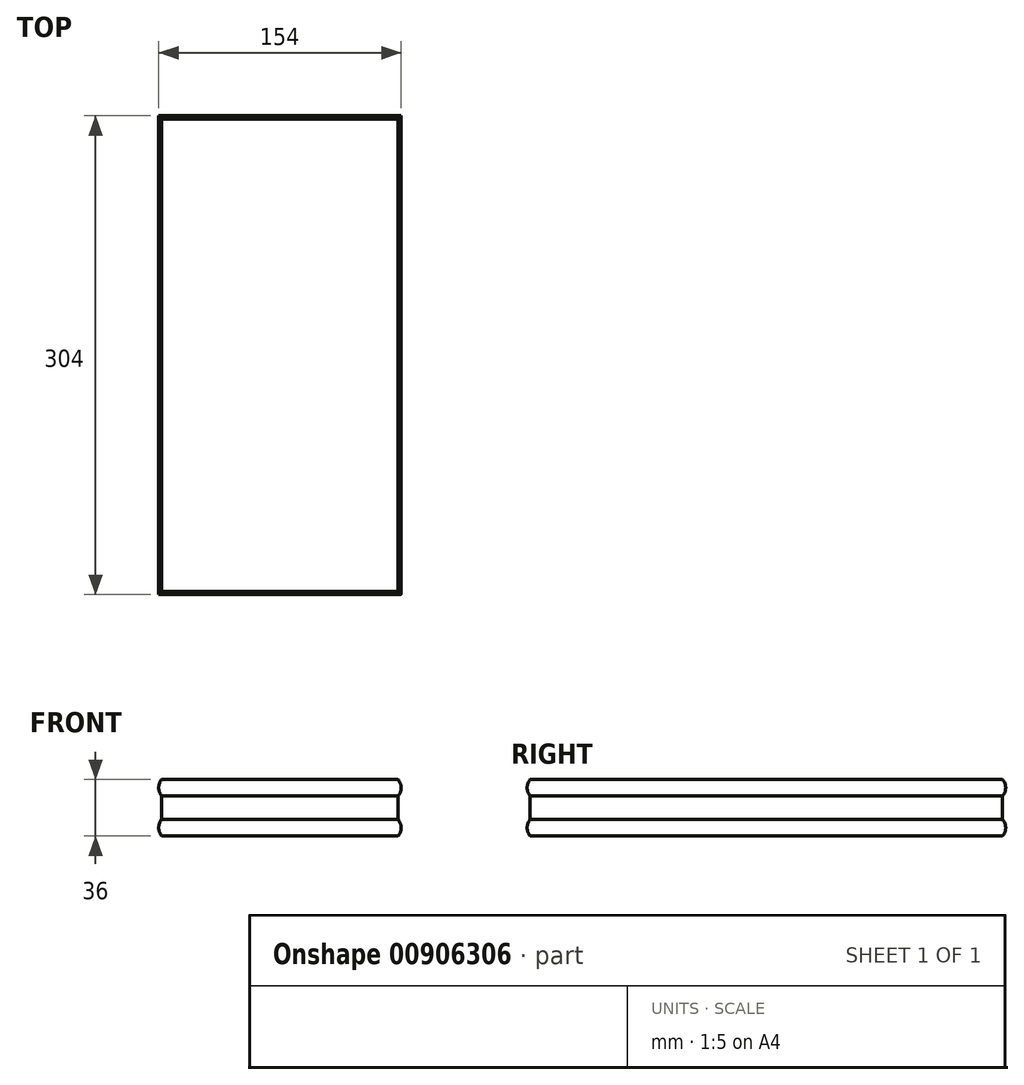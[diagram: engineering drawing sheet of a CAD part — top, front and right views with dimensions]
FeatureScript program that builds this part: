
annotation { "Feature Type Name" : "Feature", "Feature Type Description" : "" }
export const myFeature = defineFeature(function(context is Context, id is Id, definition is map)
    precondition{}
    {
        {
            var Q0;
            Q0=qCreatedBy(makeId("Top.planeOp"),FACE);
            var sketch = newSketch(context, id + "F0", { "sketchPlane" : qUnion([Q0])});
            skLineSegment(sketch, "E0.bottom", {"start": v(-75, -50) * mm, "end": v(75, -50) * mm});
            skLineSegment(sketch, "E0.top", {"start": v(-75, 250) * mm, "end": v(75, 250) * mm});
            skLineSegment(sketch, "E0.left", {"start": v(-75, -50) * mm, "end": v(-75, 250) * mm});
            skLineSegment(sketch, "E0.right", {"start": v(75, -50) * mm, "end": v(75, 250) * mm});
            skSolve(sketch);
        }
        {
            var Q0;
            Q0=qCreatedBy(makeId("Front.planeOp"),FACE);
            var sketch = newSketch(context, id + "F1", { "sketchPlane" : qUnion([Q0])});
            skLineSegment(sketch, "E1", {"start": v(-75, 0) * mm, "end": v(-75, 36) * mm});
            skLineSegment(sketch, "E2", {"start": v(-75, 0) * mm, "end": v(0, 0) * mm});
            skLineSegment(sketch, "E3", {"start": v(0, 0) * mm, "end": v(0, 36) * mm});
            skLineSegment(sketch, "E4", {"start": v(0, 36) * mm, "end": v(-75, 36) * mm});
            skArc(sketch, "E5", {"start": v(-75, 10.58) * mm, "mid": v(-77, 5.3) * mm, "end": v(-75, 0) * mm});
            skArc(sketch, "E6", {"start": v(-75, 36) * mm, "mid": v(-77, 30.7) * mm, "end": v(-75, 25.42) * mm});
            skSolve(sketch);
        }
        {
            var Q0;
            {var subQ0=sQuery(id+"F1.wireOp",EDGE,"E2");Q0=makeQuery(id+"F1.imprint","IMPRINT",FACE,{"disambiguationData":[TD([[makeQuery(id+"F1.imprint","IMPRINT",EDGE,{"derivedFrom":subQ0}),1.0]])]});}
            var Q1;
            {var subQ0=sQuery(id+"F1.wireOp",EDGE,"E6");Q1=makeQuery(id+"F1.imprint","IMPRINT",FACE,{"disambiguationData":[TD([[makeQuery(id+"F1.imprint","IMPRINT",EDGE,{"derivedFrom":subQ0}),1.0]])]});}
            var Q2;
            {var subQ0=sQuery(id+"F1.wireOp",EDGE,"E5");Q2=makeQuery(id+"F1.imprint","IMPRINT",FACE,{"disambiguationData":[TD([[makeQuery(id+"F1.imprint","IMPRINT",EDGE,{"derivedFrom":subQ0}),1.0]])]});}
            var Q3;
            Q3=sQuery(id+"F0.wireOp",EDGE,"E0.left");
            var Q4;
            Q4=sQuery(id+"F0.wireOp",EDGE,"E0.bottom");
            var Q5;
            Q5=sQuery(id+"F0.wireOp",EDGE,"E0.right");
            var Q6;
            Q6=sQuery(id+"F0.wireOp",EDGE,"E0.top");
            sweep(context, id + "F2", {"profiles" : qUnion([Q0, Q1, Q2]), "path" : qUnion([Q3, Q4, Q5, Q6])});
        }
    });
